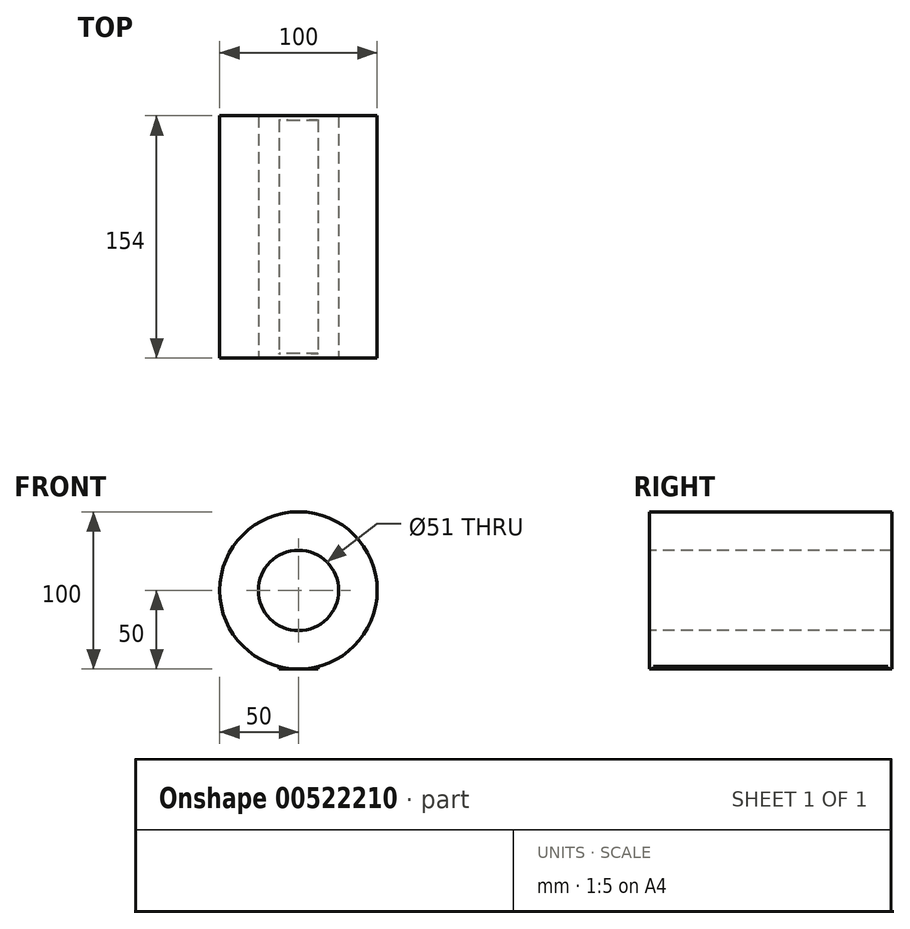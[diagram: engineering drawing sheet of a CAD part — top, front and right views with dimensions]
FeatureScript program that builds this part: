
annotation { "Feature Type Name" : "Feature", "Feature Type Description" : "" }
export const myFeature = defineFeature(function(context is Context, id is Id, definition is map)
    precondition{}
    {
        {
            var Q0;
            Q0=qCreatedBy(makeId("Right.planeOp"),FACE);
            var sketch = newSketch(context, id + "F0", { "sketchPlane" : qUnion([Q0])});
            skLineSegment(sketch, "E0", {"start": v(-77, 80) * mm, "end": v(-77, 180) * mm});
            skLineSegment(sketch, "E1", {"start": v(-77, 180) * mm, "end": v(77, 180) * mm});
            skLineSegment(sketch, "E2", {"start": v(77, 180) * mm, "end": v(77, 80) * mm});
            skLineSegment(sketch, "E3", {"start": v(77, 80) * mm, "end": v(-77, 80) * mm});
            skLineSegment(sketch, "E4", {"start": v(-77, 90.85) * mm, "end": v(-48.2, -13.33) * mm});
            skLineSegment(sketch, "E5", {"start": v(77, 90.85) * mm, "end": v(48.2, -13.33) * mm});
            skArc(sketch, "E6", {"start": v(48.2, -13.33) * mm, "mid": v(0, -50) * mm, "end": v(-48.2, -13.33) * mm});
            skCircle(sketch, "E7", {"center": v(0, 0) * mm, "radius": 20 * mm});
            skLineSegment(sketch, "E8", {"start": v(-77, 155.5) * mm, "end": v(77, 155.5) * mm});
            skLineSegment(sketch, "E9", {"start": v(-77, 104.5) * mm, "end": v(77, 104.5) * mm});
            skLineSegment(sketch, "E10", {"start": v(-77, 130) * mm, "end": v(77, 130) * mm});
            skSolve(sketch);
        }
        {
            var Q0;
            {var subQ0=sQuery(id+"F0.wireOp",EDGE,"E6");Q0=makeQuery(id+"F0.imprint","IMPRINT",FACE,{"disambiguationData":[TD([[makeQuery(id+"F0.imprint","IMPRINT",EDGE,{"derivedFrom":subQ0}),-1.0]])]});}
            var Q1;
            {var subQ7=sQuery(id+"F0.wireOp",EDGE,"E9");Q1=makeQuery(id+"F0.imprint","IMPRINT",FACE,{"disambiguationData":[TD([[makeQuery(id+"F0.imprint","IMPRINT",EDGE,{"derivedFrom":subQ7}),-1.0]])]});}
            extrude(context, id + "F1", {"entities" : qUnion([Q0, Q1]), "endBound" : BoundingType.SYMMETRIC, "depth" : 25 * mm, "offsetDistance" : 25 * mm});
        }
        {
            var Q0;
            {var subQ0=sQuery(id+"F0.wireOp",EDGE,"E1");Q0=makeQuery(id+"F0.imprint","IMPRINT",FACE,{"disambiguationData":[TD([[makeQuery(id+"F0.imprint","IMPRINT",EDGE,{"derivedFrom":subQ0}),-1.0]])]});}
            var Q1;
            Q1=sQuery(id+"F0.wireOp",EDGE,"E10");
            revolve(context, id + "F2", {"operationType" : NewBodyOperationType.ADD, "entities" : qUnion([Q0]), "axis" : qUnion([Q1]), "revolveType" : RevolveType.FULL});
        }
    });
